# Revit family: Sanitary_Taps-And-Mixers_Sanindusa_New-Icone-Bidet-Mixer
name_source: partatom
category: Plumbing Fixtures
revit_build: Autodesk Revit 2018 (Build: 20170223_1515(x64)
units: mm (PartAtom-declared; Revit-internal decimal feet)

## family parameters
Always vertical = Yes
Cut with Voids When Loaded = No
OmniClass Number = 23.45.00.00
OmniClass Title = Sanitary, Laundry, and Cleaning Equipment
Part Type = Normal
Room Calculation Point = No
Round Connector Dimension = Use Diameter
Shared = No
Work Plane-Based = No

## types (1)
- Sanitary_Taps-And-Mixers_Sanindusa_New-Icone-Bidet-Mixer
    AssetType = Fixed
    BodyMaterial = Brass
    CartridgeType = D35 mm open ceramic cartridge
    Color = Silver
    Constituents = Single lever bidet mixer. ABS/metalic D63mm pop up waste. Fixing kit. 2 x M10x1-3/8 T stainless steel flexible supply hoses.
    Cost = 0 $
    Description = New Ícone single lever bidet mixer with pop up waste
    Edition number = 1
    Element Type = FAUCET: A small diameter valve, with a free outlet, from which water is drawn.
    FaucetFunction = Mixed
    FaucetOperation = Other
    FaucetTopDescription = Single lever
    FaucetType = SprayMixing
    Features = Ceramic cartridge technology. Single lever mixer with pop up waste to install on the basin. With possibility to aplly flow rate limiter to 5L/min at 3 bar.
    Finish = Chrome plated
    FlowCoefficient = water flow to 3 bar**: 16.8L/min.
(** total opening at 50% hot water + 50% cold water)
    FlowRateMaximum = 17 L/min at 3 bar
    InletConnectionType = 2 x M10x1-3/8 stainless steel flexible supply hoses
    InstallationDate = 1900-12-31T23:59:59
    Manufacturer = Sanindusa
    ManufacturerName = Sanindusa
    ManufacturerURL = www.tec.sanindusa.pt
    Material = Brass
    ModelNumber = 526040011
    ModelReference = New Ícone
    Name = New ícone bidet mixer
    NominalHeight = 153 mm  [stored 0.501969 ft]
    NominalLength = 45 mm  [stored 0.147638 ft]
    NominalWidth = 170 mm  [stored 0.557743 ft]
    OperatingMechanismMaterial = Brass
    Pre-defined type (IFC) = FAUCET
    Product Guid = 49e32264-1b08-480d-8178-9f1371af351c
    Product data url = https://bimobject.com
    ProductInformation = https://www.tec.sanindusa.pt
    ProductionYear = 2017
    Size = 45x170x153
    TestPressure = 10 bar
    Type (IFC) = IfcValveType
    URL = www.tec.sanindusa.pt
    Uniclass2015Version = Products v1.6
    ValveMechanism = UNSET
    ValveOperation = OTHER
    ValvePattern = UNSET
    Version = 2
    WarrantyDescription = https://www.tec.sanindusa.pt
    WarrantyDurationParts = 5
    WarrantyDurationUnit = year
    WarrantyStartDate = 1900-12-31T23:59:59
1900-12-31T23:59:59
    Weight = 1.41 kg
    WorkingPressure = 0.5 - 3 bar

note: [stored X ft] marks values corroborated as IEEE doubles in the binary element streams (Revit-internal decimal feet)

## geometry (parser evidence)
native form markers: Sweep x5
no freeform markers — native parametric forms only
